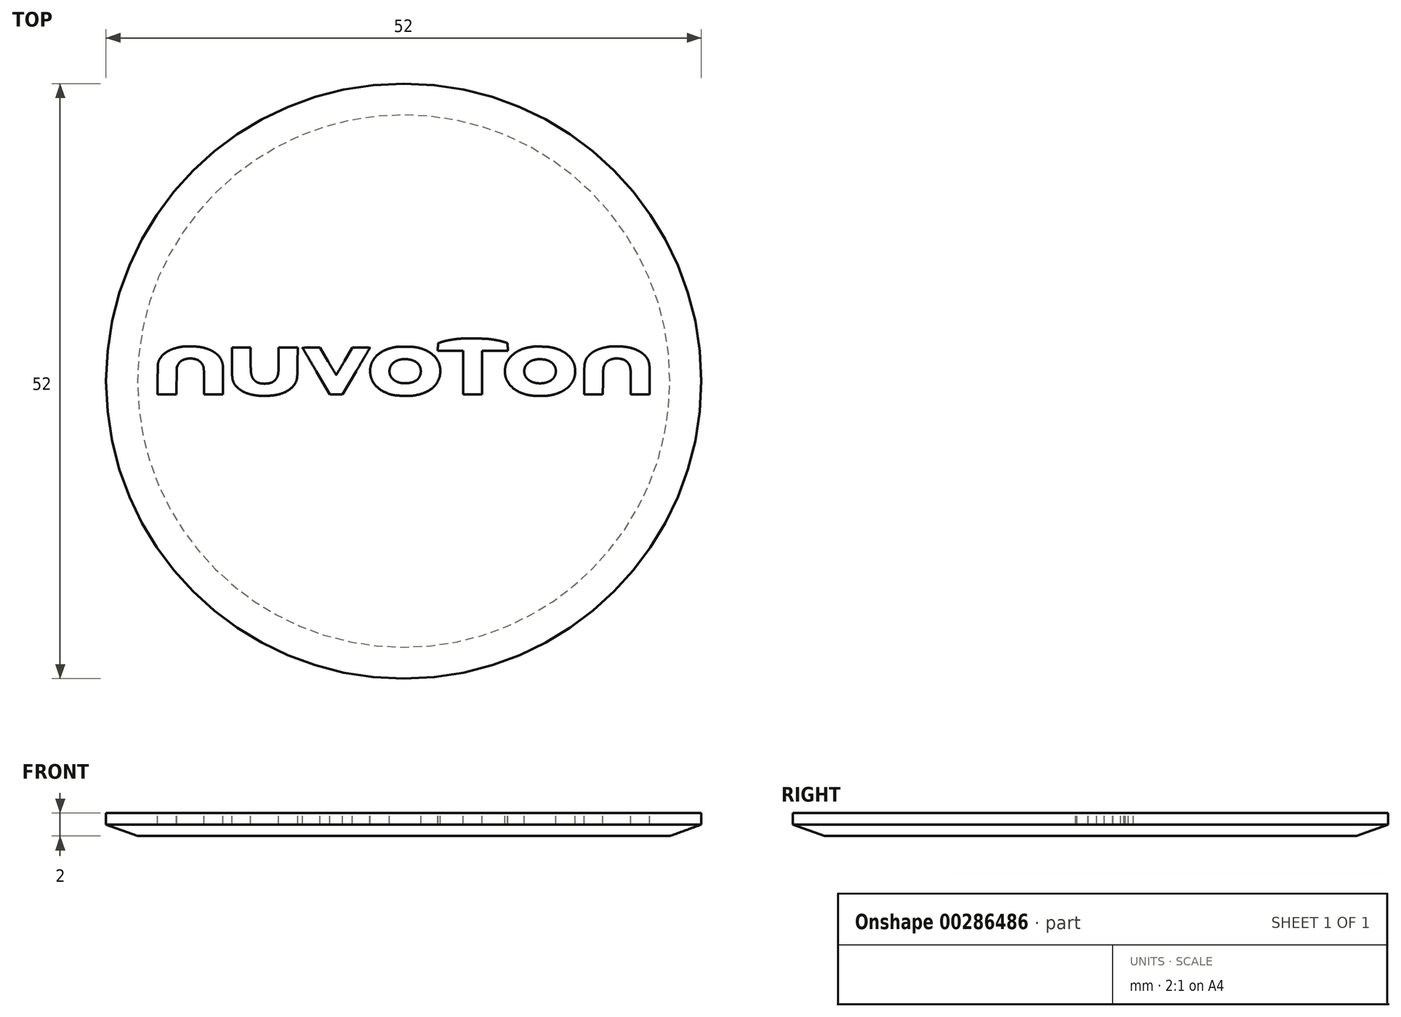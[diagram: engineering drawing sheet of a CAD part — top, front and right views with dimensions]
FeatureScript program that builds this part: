
annotation { "Feature Type Name" : "Feature", "Feature Type Description" : "" }
export const myFeature = defineFeature(function(context is Context, id is Id, definition is map)
    precondition{}
    {
        {
            var Q0;
            Q0=qCreatedBy(makeId("Top.planeOp"),FACE);
            var sketch = newSketch(context, id + "F0", { "sketchPlane" : qUnion([Q0])});
            skCircle(sketch, "E0", {"center": v(0, 0) * mm, "radius": 26 * mm});
            skSolve(sketch);
        }
        {
            var Q0;
            Q0 = qSketchRegion(id + "F0", true);
            extrude(context, id + "F1", {"entities" : qUnion([Q0]), "depth" : 2 * mm, "offsetDistance" : 25 * mm});
        }
        {
            var Q0;
            Q0=makeQuery(id+"F1.opExtrude","CAP_EDGE",EDGE,{"disambiguationData":[OSD([sQuery(id+"F0.wireOp",EDGE,"E0")])],"isStart":true});
            chamfer(context, id + "F2", {"entities" : qUnion([Q0]), "chamferType" : ChamferType.OFFSET_ANGLE, "width" : 1 * mm, "oppositeDirection" : false, "angle" : 70 * degree, "tangentPropagation" : true});
        }
        {
            var Q0;
            Q0=makeQuery(id+"F1.opExtrude","CAP_FACE",FACE,{"disambiguationData":[OSD([sQuery(id+"F0.wireOp",EDGE,"E0")])],"isStart":false});
            var sketch = newSketch(context, id + "F3", { "sketchPlane" : qUnion([Q0])});
            skArc(sketch, "E1", {"start": v(4.94, 3.7) * mm, "mid": v(4.7, 3.68) * mm, "end": v(4.45, 3.65) * mm});
            skArc(sketch, "E2", {"start": v(4.45, 3.65) * mm, "mid": v(4.22, 3.62) * mm, "end": v(4, 3.58) * mm});
            skArc(sketch, "E3", {"start": v(4, 3.58) * mm, "mid": v(3.78, 3.54) * mm, "end": v(3.58, 3.5) * mm});
            skArc(sketch, "E4", {"start": v(3.58, 3.5) * mm, "mid": v(3.4, 3.44) * mm, "end": v(3.22, 3.39) * mm});
            skLineSegment(sketch, "E5", {"start": v(3.22, 3.39) * mm, "end": v(3, 3.31) * mm});
            skLineSegment(sketch, "E6", {"start": v(3, 3.31) * mm, "end": v(3, 2.98) * mm});
            skLineSegment(sketch, "E7", {"start": v(3, 2.98) * mm, "end": v(2.99, 2.64) * mm});
            skLineSegment(sketch, "E8", {"start": v(2.99, 2.64) * mm, "end": v(4.1, 2.64) * mm});
            skLineSegment(sketch, "E9", {"start": v(4.1, 2.64) * mm, "end": v(5.2, 2.64) * mm});
            skLineSegment(sketch, "E10", {"start": v(5.2, 2.64) * mm, "end": v(5.2, 0.74) * mm});
            skLineSegment(sketch, "E11", {"start": v(5.2, 0.74) * mm, "end": v(5.2, -1.17) * mm});
            skLineSegment(sketch, "E12", {"start": v(5.2, -1.17) * mm, "end": v(6.04, -1.17) * mm});
            skLineSegment(sketch, "E13", {"start": v(6.04, -1.17) * mm, "end": v(6.87, -1.17) * mm});
            skLineSegment(sketch, "E14", {"start": v(6.87, -1.17) * mm, "end": v(6.87, 0.74) * mm});
            skLineSegment(sketch, "E15", {"start": v(6.87, 0.74) * mm, "end": v(6.87, 2.64) * mm});
            skLineSegment(sketch, "E16", {"start": v(6.87, 2.64) * mm, "end": v(7.98, 2.64) * mm});
            skLineSegment(sketch, "E17", {"start": v(7.98, 2.64) * mm, "end": v(9.09, 2.64) * mm});
            skLineSegment(sketch, "E18", {"start": v(9.09, 2.64) * mm, "end": v(9.08, 2.98) * mm});
            skLineSegment(sketch, "E19", {"start": v(9.08, 2.98) * mm, "end": v(9.07, 3.32) * mm});
            skLineSegment(sketch, "E20", {"start": v(9.07, 3.32) * mm, "end": v(8.82, 3.4) * mm});
            skArc(sketch, "E21", {"start": v(8.82, 3.4) * mm, "mid": v(8.7, 3.44) * mm, "end": v(8.56, 3.48) * mm});
            skArc(sketch, "E22", {"start": v(8.56, 3.48) * mm, "mid": v(8.41, 3.51) * mm, "end": v(8.26, 3.55) * mm});
            skArc(sketch, "E23", {"start": v(8.26, 3.55) * mm, "mid": v(8.09, 3.58) * mm, "end": v(7.92, 3.6) * mm});
            skArc(sketch, "E24", {"start": v(7.92, 3.6) * mm, "mid": v(7.74, 3.64) * mm, "end": v(7.55, 3.66) * mm});
            skArc(sketch, "E25", {"start": v(7.55, 3.66) * mm, "mid": v(7.32, 3.69) * mm, "end": v(7.09, 3.7) * mm});
            skArc(sketch, "E26", {"start": v(7.09, 3.7) * mm, "mid": v(6.68, 3.71) * mm, "end": v(6.26, 3.72) * mm});
            skArc(sketch, "E27", {"start": v(6.26, 3.72) * mm, "mid": v(5.85, 3.73) * mm, "end": v(5.44, 3.73) * mm});
            skArc(sketch, "E28", {"start": v(5.44, 3.73) * mm, "mid": v(5.19, 3.72) * mm, "end": v(4.94, 3.7) * mm});
            skArc(sketch, "E29", {"start": v(-19.23, 3.02) * mm, "mid": v(-19.63, 2.95) * mm, "end": v(-20.03, 2.85) * mm});
            skArc(sketch, "E30", {"start": v(-20.03, 2.85) * mm, "mid": v(-20.35, 2.74) * mm, "end": v(-20.66, 2.58) * mm});
            skArc(sketch, "E31", {"start": v(-20.66, 2.58) * mm, "mid": v(-20.9, 2.4) * mm, "end": v(-21.12, 2.2) * mm});
            skArc(sketch, "E32", {"start": v(-21.12, 2.2) * mm, "mid": v(-21.3, 1.97) * mm, "end": v(-21.41, 1.71) * mm});
            skArc(sketch, "E33", {"start": v(-21.41, 1.71) * mm, "mid": v(-21.44, 1.64) * mm, "end": v(-21.45, 1.56) * mm});
            skArc(sketch, "E34", {"start": v(-21.45, 1.56) * mm, "mid": v(-21.47, 1.47) * mm, "end": v(-21.47, 1.37) * mm});
            skArc(sketch, "E35", {"start": v(-21.47, 1.37) * mm, "mid": v(-21.48, 1.2) * mm, "end": v(-21.48, 1.03) * mm});
            skArc(sketch, "E36", {"start": v(-21.48, 1.03) * mm, "mid": v(-21.49, 0.6) * mm, "end": v(-21.5, 0.18) * mm});
            skLineSegment(sketch, "E37", {"start": v(-21.5, 0.18) * mm, "end": v(-21.5, -1.17) * mm});
            skLineSegment(sketch, "E38", {"start": v(-21.5, -1.17) * mm, "end": v(-20.67, -1.17) * mm});
            skLineSegment(sketch, "E39", {"start": v(-20.67, -1.17) * mm, "end": v(-19.84, -1.17) * mm});
            skLineSegment(sketch, "E40", {"start": v(-19.84, -1.17) * mm, "end": v(-19.83, 0.01) * mm});
            skLineSegment(sketch, "E41", {"start": v(-19.83, 0.01) * mm, "end": v(-19.82, 1.2) * mm});
            skLineSegment(sketch, "E42", {"start": v(-19.82, 1.2) * mm, "end": v(-19.72, 1.4) * mm});
            skArc(sketch, "E43", {"start": v(-19.72, 1.4) * mm, "mid": v(-19.7, 1.44) * mm, "end": v(-19.67, 1.49) * mm});
            skArc(sketch, "E44", {"start": v(-19.67, 1.49) * mm, "mid": v(-19.65, 1.53) * mm, "end": v(-19.62, 1.57) * mm});
            skArc(sketch, "E45", {"start": v(-19.62, 1.57) * mm, "mid": v(-19.6, 1.61) * mm, "end": v(-19.56, 1.65) * mm});
            skArc(sketch, "E46", {"start": v(-19.56, 1.65) * mm, "mid": v(-19.54, 1.67) * mm, "end": v(-19.52, 1.7) * mm});
            skArc(sketch, "E47", {"start": v(-19.52, 1.7) * mm, "mid": v(-19.41, 1.77) * mm, "end": v(-19.3, 1.84) * mm});
            skArc(sketch, "E48", {"start": v(-19.3, 1.84) * mm, "mid": v(-19.16, 1.9) * mm, "end": v(-19.02, 1.93) * mm});
            skArc(sketch, "E49", {"start": v(-19.02, 1.93) * mm, "mid": v(-18.87, 1.96) * mm, "end": v(-18.72, 1.98) * mm});
            skArc(sketch, "E50", {"start": v(-18.72, 1.98) * mm, "mid": v(-18.57, 1.98) * mm, "end": v(-18.42, 1.96) * mm});
            skArc(sketch, "E51", {"start": v(-18.42, 1.96) * mm, "mid": v(-18.3, 1.94) * mm, "end": v(-18.19, 1.91) * mm});
            skArc(sketch, "E52", {"start": v(-18.19, 1.91) * mm, "mid": v(-18.1, 1.89) * mm, "end": v(-18, 1.85) * mm});
            skArc(sketch, "E53", {"start": v(-18, 1.85) * mm, "mid": v(-17.93, 1.8) * mm, "end": v(-17.86, 1.76) * mm});
            skArc(sketch, "E54", {"start": v(-17.86, 1.76) * mm, "mid": v(-17.78, 1.7) * mm, "end": v(-17.72, 1.63) * mm});
            skArc(sketch, "E55", {"start": v(-17.72, 1.63) * mm, "mid": v(-17.63, 1.52) * mm, "end": v(-17.56, 1.41) * mm});
            skArc(sketch, "E56", {"start": v(-17.56, 1.41) * mm, "mid": v(-17.51, 1.31) * mm, "end": v(-17.48, 1.2) * mm});
            skArc(sketch, "E57", {"start": v(-17.48, 1.2) * mm, "mid": v(-17.46, 1.04) * mm, "end": v(-17.45, 0.87) * mm});
            skArc(sketch, "E58", {"start": v(-17.45, 0.87) * mm, "mid": v(-17.44, 0.43) * mm, "end": v(-17.44, 0) * mm});
            skLineSegment(sketch, "E59", {"start": v(-17.44, 0) * mm, "end": v(-17.43, -1.17) * mm});
            skLineSegment(sketch, "E60", {"start": v(-17.43, -1.17) * mm, "end": v(-16.6, -1.17) * mm});
            skLineSegment(sketch, "E61", {"start": v(-16.6, -1.17) * mm, "end": v(-15.77, -1.17) * mm});
            skLineSegment(sketch, "E62", {"start": v(-15.77, -1.17) * mm, "end": v(-15.78, 0.03) * mm});
            skArc(sketch, "E63", {"start": v(-15.78, 0.03) * mm, "mid": v(-15.78, 0.26) * mm, "end": v(-15.78, 0.5) * mm});
            skArc(sketch, "E64", {"start": v(-15.78, 0.5) * mm, "mid": v(-15.78, 0.72) * mm, "end": v(-15.78, 0.93) * mm});
            skArc(sketch, "E65", {"start": v(-15.78, 0.93) * mm, "mid": v(-15.79, 1.11) * mm, "end": v(-15.8, 1.3) * mm});
            skArc(sketch, "E66", {"start": v(-15.8, 1.3) * mm, "mid": v(-15.8, 1.37) * mm, "end": v(-15.8, 1.43) * mm});
            skArc(sketch, "E67", {"start": v(-15.8, 1.43) * mm, "mid": v(-15.85, 1.63) * mm, "end": v(-15.91, 1.81) * mm});
            skArc(sketch, "E68", {"start": v(-15.91, 1.81) * mm, "mid": v(-16, 1.99) * mm, "end": v(-16.12, 2.15) * mm});
            skArc(sketch, "E69", {"start": v(-16.12, 2.15) * mm, "mid": v(-16.26, 2.3) * mm, "end": v(-16.42, 2.44) * mm});
            skArc(sketch, "E70", {"start": v(-16.42, 2.44) * mm, "mid": v(-16.61, 2.56) * mm, "end": v(-16.81, 2.67) * mm});
            skArc(sketch, "E71", {"start": v(-16.81, 2.67) * mm, "mid": v(-17, 2.76) * mm, "end": v(-17.2, 2.83) * mm});
            skArc(sketch, "E72", {"start": v(-17.2, 2.83) * mm, "mid": v(-17.39, 2.9) * mm, "end": v(-17.58, 2.94) * mm});
            skArc(sketch, "E73", {"start": v(-17.58, 2.94) * mm, "mid": v(-17.8, 2.98) * mm, "end": v(-18.01, 3) * mm});
            skArc(sketch, "E74", {"start": v(-18.01, 3) * mm, "mid": v(-18.27, 3.02) * mm, "end": v(-18.53, 3.04) * mm});
            skArc(sketch, "E75", {"start": v(-18.53, 3.04) * mm, "mid": v(-18.63, 3.04) * mm, "end": v(-18.73, 3.04) * mm});
            skArc(sketch, "E76", {"start": v(-18.73, 3.04) * mm, "mid": v(-18.83, 3.04) * mm, "end": v(-18.93, 3.04) * mm});
            skArc(sketch, "E77", {"start": v(-18.93, 3.04) * mm, "mid": v(-19.02, 3.03) * mm, "end": v(-19.12, 3.03) * mm});
            skArc(sketch, "E78", {"start": v(-19.12, 3.03) * mm, "mid": v(-19.17, 3.03) * mm, "end": v(-19.23, 3.02) * mm});
            skArc(sketch, "E79", {"start": v(18.05, 3.02) * mm, "mid": v(17.84, 3) * mm, "end": v(17.63, 2.95) * mm});
            skArc(sketch, "E80", {"start": v(17.63, 2.95) * mm, "mid": v(17.44, 2.9) * mm, "end": v(17.24, 2.85) * mm});
            skArc(sketch, "E81", {"start": v(17.24, 2.85) * mm, "mid": v(17.07, 2.8) * mm, "end": v(16.9, 2.73) * mm});
            skArc(sketch, "E82", {"start": v(16.9, 2.73) * mm, "mid": v(16.75, 2.66) * mm, "end": v(16.6, 2.58) * mm});
            skArc(sketch, "E83", {"start": v(16.6, 2.58) * mm, "mid": v(16.51, 2.52) * mm, "end": v(16.42, 2.45) * mm});
            skArc(sketch, "E84", {"start": v(16.42, 2.45) * mm, "mid": v(16.33, 2.37) * mm, "end": v(16.23, 2.28) * mm});
            skArc(sketch, "E85", {"start": v(16.23, 2.28) * mm, "mid": v(16.15, 2.2) * mm, "end": v(16.07, 2.1) * mm});
            skArc(sketch, "E86", {"start": v(16.07, 2.1) * mm, "mid": v(16, 2.02) * mm, "end": v(15.96, 1.94) * mm});
            skArc(sketch, "E87", {"start": v(15.96, 1.94) * mm, "mid": v(15.9, 1.82) * mm, "end": v(15.86, 1.7) * mm});
            skArc(sketch, "E88", {"start": v(15.86, 1.7) * mm, "mid": v(15.82, 1.57) * mm, "end": v(15.8, 1.44) * mm});
            skArc(sketch, "E89", {"start": v(15.8, 1.44) * mm, "mid": v(15.79, 1.24) * mm, "end": v(15.78, 1.04) * mm});
            skArc(sketch, "E90", {"start": v(15.78, 1.04) * mm, "mid": v(15.78, 0.58) * mm, "end": v(15.78, 0.12) * mm});
            skLineSegment(sketch, "E91", {"start": v(15.78, 0.12) * mm, "end": v(15.78, -1.17) * mm});
            skLineSegment(sketch, "E92", {"start": v(15.78, -1.17) * mm, "end": v(16.59, -1.17) * mm});
            skLineSegment(sketch, "E93", {"start": v(16.59, -1.17) * mm, "end": v(17.4, -1.17) * mm});
            skLineSegment(sketch, "E94", {"start": v(17.4, -1.17) * mm, "end": v(17.41, -0.04) * mm});
            skArc(sketch, "E95", {"start": v(17.41, -0.04) * mm, "mid": v(17.42, 0.37) * mm, "end": v(17.43, 0.78) * mm});
            skArc(sketch, "E96", {"start": v(17.43, 0.78) * mm, "mid": v(17.44, 0.96) * mm, "end": v(17.45, 1.14) * mm});
            skArc(sketch, "E97", {"start": v(17.45, 1.14) * mm, "mid": v(17.48, 1.25) * mm, "end": v(17.52, 1.36) * mm});
            skArc(sketch, "E98", {"start": v(17.52, 1.36) * mm, "mid": v(17.57, 1.46) * mm, "end": v(17.63, 1.56) * mm});
            skArc(sketch, "E99", {"start": v(17.63, 1.56) * mm, "mid": v(17.7, 1.64) * mm, "end": v(17.79, 1.72) * mm});
            skArc(sketch, "E100", {"start": v(17.79, 1.72) * mm, "mid": v(17.88, 1.78) * mm, "end": v(17.97, 1.84) * mm});
            skArc(sketch, "E101", {"start": v(17.97, 1.84) * mm, "mid": v(18.08, 1.89) * mm, "end": v(18.2, 1.92) * mm});
            skArc(sketch, "E102", {"start": v(18.2, 1.92) * mm, "mid": v(18.33, 1.95) * mm, "end": v(18.47, 1.97) * mm});
            skArc(sketch, "E103", {"start": v(18.47, 1.97) * mm, "mid": v(18.56, 1.98) * mm, "end": v(18.65, 1.98) * mm});
            skArc(sketch, "E104", {"start": v(18.65, 1.98) * mm, "mid": v(18.76, 1.97) * mm, "end": v(18.86, 1.96) * mm});
            skArc(sketch, "E105", {"start": v(18.86, 1.96) * mm, "mid": v(18.97, 1.94) * mm, "end": v(19.08, 1.92) * mm});
            skArc(sketch, "E106", {"start": v(19.08, 1.92) * mm, "mid": v(19.16, 1.9) * mm, "end": v(19.23, 1.87) * mm});
            skArc(sketch, "E107", {"start": v(19.23, 1.87) * mm, "mid": v(19.3, 1.83) * mm, "end": v(19.37, 1.79) * mm});
            skArc(sketch, "E108", {"start": v(19.37, 1.79) * mm, "mid": v(19.44, 1.74) * mm, "end": v(19.5, 1.68) * mm});
            skArc(sketch, "E109", {"start": v(19.5, 1.68) * mm, "mid": v(19.56, 1.62) * mm, "end": v(19.62, 1.55) * mm});
            skArc(sketch, "E110", {"start": v(19.62, 1.55) * mm, "mid": v(19.66, 1.5) * mm, "end": v(19.7, 1.43) * mm});
            skArc(sketch, "E111", {"start": v(19.7, 1.43) * mm, "mid": v(19.74, 1.33) * mm, "end": v(19.78, 1.22) * mm});
            skArc(sketch, "E112", {"start": v(19.78, 1.22) * mm, "mid": v(19.8, 1.1) * mm, "end": v(19.82, 0.97) * mm});
            skArc(sketch, "E113", {"start": v(19.82, 0.97) * mm, "mid": v(19.83, 0.78) * mm, "end": v(19.84, 0.6) * mm});
            skArc(sketch, "E114", {"start": v(19.84, 0.6) * mm, "mid": v(19.84, 0.23) * mm, "end": v(19.84, -0.13) * mm});
            skLineSegment(sketch, "E115", {"start": v(19.84, -0.13) * mm, "end": v(19.84, -1.17) * mm});
            skLineSegment(sketch, "E116", {"start": v(19.84, -1.17) * mm, "end": v(20.67, -1.17) * mm});
            skLineSegment(sketch, "E117", {"start": v(20.67, -1.17) * mm, "end": v(21.5, -1.17) * mm});
            skLineSegment(sketch, "E118", {"start": v(21.5, -1.17) * mm, "end": v(21.5, 0.01) * mm});
            skArc(sketch, "E119", {"start": v(21.5, 0.01) * mm, "mid": v(21.5, 0.41) * mm, "end": v(21.5, 0.81) * mm});
            skArc(sketch, "E120", {"start": v(21.5, 0.81) * mm, "mid": v(21.49, 1.03) * mm, "end": v(21.48, 1.25) * mm});
            skArc(sketch, "E121", {"start": v(21.48, 1.25) * mm, "mid": v(21.46, 1.4) * mm, "end": v(21.44, 1.54) * mm});
            skArc(sketch, "E122", {"start": v(21.44, 1.54) * mm, "mid": v(21.41, 1.66) * mm, "end": v(21.38, 1.77) * mm});
            skArc(sketch, "E123", {"start": v(21.38, 1.77) * mm, "mid": v(21.31, 1.9) * mm, "end": v(21.24, 2.04) * mm});
            skArc(sketch, "E124", {"start": v(21.24, 2.04) * mm, "mid": v(21.14, 2.16) * mm, "end": v(21.03, 2.28) * mm});
            skArc(sketch, "E125", {"start": v(21.03, 2.28) * mm, "mid": v(20.9, 2.4) * mm, "end": v(20.75, 2.5) * mm});
            skArc(sketch, "E126", {"start": v(20.75, 2.5) * mm, "mid": v(20.59, 2.6) * mm, "end": v(20.42, 2.7) * mm});
            skArc(sketch, "E127", {"start": v(20.42, 2.7) * mm, "mid": v(20.24, 2.77) * mm, "end": v(20.05, 2.84) * mm});
            skArc(sketch, "E128", {"start": v(20.05, 2.84) * mm, "mid": v(19.87, 2.9) * mm, "end": v(19.68, 2.94) * mm});
            skArc(sketch, "E129", {"start": v(19.68, 2.94) * mm, "mid": v(19.46, 2.98) * mm, "end": v(19.25, 3) * mm});
            skArc(sketch, "E130", {"start": v(19.25, 3) * mm, "mid": v(19, 3.02) * mm, "end": v(18.75, 3.04) * mm});
            skArc(sketch, "E131", {"start": v(18.75, 3.04) * mm, "mid": v(18.65, 3.04) * mm, "end": v(18.55, 3.04) * mm});
            skArc(sketch, "E132", {"start": v(18.55, 3.04) * mm, "mid": v(18.45, 3.04) * mm, "end": v(18.34, 3.04) * mm});
            skArc(sketch, "E133", {"start": v(18.34, 3.04) * mm, "mid": v(18.25, 3.03) * mm, "end": v(18.16, 3.03) * mm});
            skArc(sketch, "E134", {"start": v(18.16, 3.03) * mm, "mid": v(18.1, 3.03) * mm, "end": v(18.05, 3.02) * mm});
            skArc(sketch, "E135", {"start": v(-0.66, 2.99) * mm, "mid": v(-1.13, 2.88) * mm, "end": v(-1.6, 2.72) * mm});
            skArc(sketch, "E136", {"start": v(-1.6, 2.72) * mm, "mid": v(-1.97, 2.52) * mm, "end": v(-2.32, 2.26) * mm});
            skArc(sketch, "E137", {"start": v(-2.32, 2.26) * mm, "mid": v(-2.57, 1.96) * mm, "end": v(-2.77, 1.63) * mm});
            skArc(sketch, "E138", {"start": v(-2.77, 1.63) * mm, "mid": v(-2.9, 1.26) * mm, "end": v(-2.93, 0.88) * mm});
            skArc(sketch, "E139", {"start": v(-2.93, 0.88) * mm, "mid": v(-2.9, 0.52) * mm, "end": v(-2.8, 0.17) * mm});
            skArc(sketch, "E140", {"start": v(-2.8, 0.17) * mm, "mid": v(-2.63, -0.15) * mm, "end": v(-2.4, -0.44) * mm});
            skArc(sketch, "E141", {"start": v(-2.4, -0.44) * mm, "mid": v(-2.12, -0.7) * mm, "end": v(-1.78, -0.9) * mm});
            skArc(sketch, "E142", {"start": v(-1.78, -0.9) * mm, "mid": v(-1.38, -1.08) * mm, "end": v(-0.96, -1.2) * mm});
            skArc(sketch, "E143", {"start": v(-0.96, -1.2) * mm, "mid": v(-0.79, -1.24) * mm, "end": v(-0.62, -1.26) * mm});
            skArc(sketch, "E144", {"start": v(-0.62, -1.26) * mm, "mid": v(-0.34, -1.28) * mm, "end": v(-0.06, -1.29) * mm});
            skArc(sketch, "E145", {"start": v(-0.06, -1.29) * mm, "mid": v(0.22, -1.3) * mm, "end": v(0.5, -1.3) * mm});
            skArc(sketch, "E146", {"start": v(0.5, -1.3) * mm, "mid": v(0.68, -1.29) * mm, "end": v(0.87, -1.27) * mm});
            skArc(sketch, "E147", {"start": v(0.87, -1.27) * mm, "mid": v(1.36, -1.16) * mm, "end": v(1.84, -1) * mm});
            skArc(sketch, "E148", {"start": v(1.84, -1) * mm, "mid": v(2.23, -0.8) * mm, "end": v(2.58, -0.54) * mm});
            skArc(sketch, "E149", {"start": v(2.58, -0.54) * mm, "mid": v(2.84, -0.24) * mm, "end": v(3.04, 0.1) * mm});
            skArc(sketch, "E150", {"start": v(3.04, 0.1) * mm, "mid": v(3.16, 0.47) * mm, "end": v(3.2, 0.86) * mm});
            skArc(sketch, "E151", {"start": v(3.2, 0.86) * mm, "mid": v(3.18, 1.18) * mm, "end": v(3.1, 1.48) * mm});
            skArc(sketch, "E152", {"start": v(3.1, 1.48) * mm, "mid": v(2.97, 1.77) * mm, "end": v(2.8, 2.03) * mm});
            skArc(sketch, "E153", {"start": v(2.8, 2.03) * mm, "mid": v(2.57, 2.28) * mm, "end": v(2.3, 2.48) * mm});
            skArc(sketch, "E154", {"start": v(2.3, 2.48) * mm, "mid": v(2, 2.66) * mm, "end": v(1.66, 2.8) * mm});
            skArc(sketch, "E155", {"start": v(1.66, 2.8) * mm, "mid": v(1.5, 2.86) * mm, "end": v(1.34, 2.9) * mm});
            skArc(sketch, "E156", {"start": v(1.34, 2.9) * mm, "mid": v(1.2, 2.93) * mm, "end": v(1.05, 2.96) * mm});
            skArc(sketch, "E157", {"start": v(1.05, 2.96) * mm, "mid": v(0.89, 2.98) * mm, "end": v(0.72, 3) * mm});
            skArc(sketch, "E158", {"start": v(0.72, 3) * mm, "mid": v(0.48, 3) * mm, "end": v(0.24, 3) * mm});
            skArc(sketch, "E159", {"start": v(0.24, 3) * mm, "mid": v(0.1, 3) * mm, "end": v(-0.05, 3) * mm});
            skArc(sketch, "E160", {"start": v(-0.05, 3) * mm, "mid": v(-0.18, 3) * mm, "end": v(-0.32, 3) * mm});
            skArc(sketch, "E161", {"start": v(-0.32, 3) * mm, "mid": v(-0.43, 3) * mm, "end": v(-0.54, 3) * mm});
            skArc(sketch, "E162", {"start": v(-0.54, 3) * mm, "mid": v(-0.6, 3) * mm, "end": v(-0.66, 2.99) * mm});
            skArc(sketch, "E163", {"start": v(0.52, 1.88) * mm, "mid": v(0.73, 1.83) * mm, "end": v(0.93, 1.75) * mm});
            skArc(sketch, "E164", {"start": v(0.93, 1.75) * mm, "mid": v(1.1, 1.66) * mm, "end": v(1.24, 1.53) * mm});
            skArc(sketch, "E165", {"start": v(1.24, 1.53) * mm, "mid": v(1.35, 1.39) * mm, "end": v(1.43, 1.23) * mm});
            skArc(sketch, "E166", {"start": v(1.43, 1.23) * mm, "mid": v(1.48, 1.05) * mm, "end": v(1.5, 0.86) * mm});
            skArc(sketch, "E167", {"start": v(1.5, 0.86) * mm, "mid": v(1.48, 0.65) * mm, "end": v(1.42, 0.45) * mm});
            skArc(sketch, "E168", {"start": v(1.42, 0.45) * mm, "mid": v(1.31, 0.27) * mm, "end": v(1.17, 0.13) * mm});
            skArc(sketch, "E169", {"start": v(1.17, 0.13) * mm, "mid": v(0.99, 0) * mm, "end": v(0.78, -0.1) * mm});
            skArc(sketch, "E170", {"start": v(0.78, -0.1) * mm, "mid": v(0.52, -0.16) * mm, "end": v(0.26, -0.19) * mm});
            skArc(sketch, "E171", {"start": v(0.26, -0.19) * mm, "mid": v(0.02, -0.2) * mm, "end": v(-0.21, -0.17) * mm});
            skArc(sketch, "E172", {"start": v(-0.21, -0.17) * mm, "mid": v(-0.42, -0.12) * mm, "end": v(-0.62, -0.04) * mm});
            skArc(sketch, "E173", {"start": v(-0.62, -0.04) * mm, "mid": v(-0.8, 0.05) * mm, "end": v(-0.94, 0.17) * mm});
            skArc(sketch, "E174", {"start": v(-0.94, 0.17) * mm, "mid": v(-1.07, 0.3) * mm, "end": v(-1.16, 0.47) * mm});
            skArc(sketch, "E175", {"start": v(-1.16, 0.47) * mm, "mid": v(-1.2, 0.56) * mm, "end": v(-1.22, 0.66) * mm});
            skArc(sketch, "E176", {"start": v(-1.22, 0.66) * mm, "mid": v(-1.24, 0.77) * mm, "end": v(-1.24, 0.88) * mm});
            skArc(sketch, "E177", {"start": v(-1.24, 0.88) * mm, "mid": v(-1.23, 0.99) * mm, "end": v(-1.21, 1.1) * mm});
            skArc(sketch, "E178", {"start": v(-1.21, 1.1) * mm, "mid": v(-1.18, 1.2) * mm, "end": v(-1.14, 1.3) * mm});
            skArc(sketch, "E179", {"start": v(-1.14, 1.3) * mm, "mid": v(-1.03, 1.47) * mm, "end": v(-0.88, 1.6) * mm});
            skArc(sketch, "E180", {"start": v(-0.88, 1.6) * mm, "mid": v(-0.7, 1.73) * mm, "end": v(-0.5, 1.82) * mm});
            skArc(sketch, "E181", {"start": v(-0.5, 1.82) * mm, "mid": v(-0.26, 1.89) * mm, "end": v(-0.02, 1.92) * mm});
            skArc(sketch, "E182", {"start": v(-0.02, 1.92) * mm, "mid": v(0.25, 1.91) * mm, "end": v(0.52, 1.88) * mm});
            skArc(sketch, "E183", {"start": v(11.27, 3) * mm, "mid": v(11.26, 3) * mm, "end": v(11.24, 3) * mm});
            skArc(sketch, "E184", {"start": v(11.24, 3) * mm, "mid": v(11.2, 3) * mm, "end": v(11.17, 2.99) * mm});
            skArc(sketch, "E185", {"start": v(11.17, 2.99) * mm, "mid": v(11.13, 2.98) * mm, "end": v(11.09, 2.97) * mm});
            skArc(sketch, "E186", {"start": v(11.09, 2.97) * mm, "mid": v(11.04, 2.96) * mm, "end": v(11, 2.96) * mm});
            skArc(sketch, "E187", {"start": v(11, 2.96) * mm, "mid": v(10.63, 2.88) * mm, "end": v(10.28, 2.76) * mm});
            skArc(sketch, "E188", {"start": v(10.28, 2.76) * mm, "mid": v(9.96, 2.6) * mm, "end": v(9.66, 2.42) * mm});
            skArc(sketch, "E189", {"start": v(9.66, 2.42) * mm, "mid": v(9.42, 2.2) * mm, "end": v(9.2, 1.96) * mm});
            skArc(sketch, "E190", {"start": v(9.2, 1.96) * mm, "mid": v(9.04, 1.7) * mm, "end": v(8.92, 1.4) * mm});
            skArc(sketch, "E191", {"start": v(8.92, 1.4) * mm, "mid": v(8.89, 1.28) * mm, "end": v(8.87, 1.15) * mm});
            skArc(sketch, "E192", {"start": v(8.87, 1.15) * mm, "mid": v(8.85, 1) * mm, "end": v(8.85, 0.85) * mm});
            skArc(sketch, "E193", {"start": v(8.85, 0.85) * mm, "mid": v(8.86, 0.7) * mm, "end": v(8.87, 0.54) * mm});
            skArc(sketch, "E194", {"start": v(8.87, 0.54) * mm, "mid": v(8.9, 0.42) * mm, "end": v(8.93, 0.3) * mm});
            skArc(sketch, "E195", {"start": v(8.93, 0.3) * mm, "mid": v(9.05, 0) * mm, "end": v(9.23, -0.26) * mm});
            skArc(sketch, "E196", {"start": v(9.23, -0.26) * mm, "mid": v(9.44, -0.5) * mm, "end": v(9.7, -0.72) * mm});
            skArc(sketch, "E197", {"start": v(9.7, -0.72) * mm, "mid": v(10, -0.9) * mm, "end": v(10.31, -1.05) * mm});
            skArc(sketch, "E198", {"start": v(10.31, -1.05) * mm, "mid": v(10.68, -1.17) * mm, "end": v(11.07, -1.25) * mm});
            skArc(sketch, "E199", {"start": v(11.07, -1.25) * mm, "mid": v(11.23, -1.27) * mm, "end": v(11.39, -1.28) * mm});
            skArc(sketch, "E200", {"start": v(11.39, -1.28) * mm, "mid": v(11.63, -1.29) * mm, "end": v(11.88, -1.3) * mm});
            skArc(sketch, "E201", {"start": v(11.88, -1.3) * mm, "mid": v(12.13, -1.3) * mm, "end": v(12.37, -1.29) * mm});
            skArc(sketch, "E202", {"start": v(12.37, -1.29) * mm, "mid": v(12.53, -1.28) * mm, "end": v(12.7, -1.26) * mm});
            skArc(sketch, "E203", {"start": v(12.7, -1.26) * mm, "mid": v(12.84, -1.24) * mm, "end": v(12.98, -1.2) * mm});
            skArc(sketch, "E204", {"start": v(12.98, -1.2) * mm, "mid": v(13.11, -1.18) * mm, "end": v(13.24, -1.14) * mm});
            skArc(sketch, "E205", {"start": v(13.24, -1.14) * mm, "mid": v(13.37, -1.1) * mm, "end": v(13.5, -1.05) * mm});
            skArc(sketch, "E206", {"start": v(13.5, -1.05) * mm, "mid": v(13.63, -1) * mm, "end": v(13.76, -0.93) * mm});
            skArc(sketch, "E207", {"start": v(13.76, -0.93) * mm, "mid": v(13.97, -0.82) * mm, "end": v(14.16, -0.7) * mm});
            skArc(sketch, "E208", {"start": v(14.16, -0.7) * mm, "mid": v(14.34, -0.56) * mm, "end": v(14.5, -0.4) * mm});
            skArc(sketch, "E209", {"start": v(14.5, -0.4) * mm, "mid": v(14.63, -0.24) * mm, "end": v(14.74, -0.07) * mm});
            skArc(sketch, "E210", {"start": v(14.74, -0.07) * mm, "mid": v(14.84, 0.12) * mm, "end": v(14.9, 0.32) * mm});
            skArc(sketch, "E211", {"start": v(14.9, 0.32) * mm, "mid": v(14.94, 0.44) * mm, "end": v(14.96, 0.57) * mm});
            skArc(sketch, "E212", {"start": v(14.96, 0.57) * mm, "mid": v(14.98, 0.71) * mm, "end": v(14.98, 0.86) * mm});
            skArc(sketch, "E213", {"start": v(14.98, 0.86) * mm, "mid": v(14.98, 1.01) * mm, "end": v(14.96, 1.16) * mm});
            skArc(sketch, "E214", {"start": v(14.96, 1.16) * mm, "mid": v(14.94, 1.29) * mm, "end": v(14.9, 1.4) * mm});
            skArc(sketch, "E215", {"start": v(14.9, 1.4) * mm, "mid": v(14.8, 1.7) * mm, "end": v(14.62, 1.97) * mm});
            skArc(sketch, "E216", {"start": v(14.62, 1.97) * mm, "mid": v(14.4, 2.22) * mm, "end": v(14.15, 2.43) * mm});
            skArc(sketch, "E217", {"start": v(14.15, 2.43) * mm, "mid": v(13.85, 2.62) * mm, "end": v(13.52, 2.77) * mm});
            skArc(sketch, "E218", {"start": v(13.52, 2.77) * mm, "mid": v(13.14, 2.89) * mm, "end": v(12.74, 2.97) * mm});
            skArc(sketch, "E219", {"start": v(12.74, 2.97) * mm, "mid": v(12.6, 2.99) * mm, "end": v(12.47, 3) * mm});
            skArc(sketch, "E220", {"start": v(12.47, 3) * mm, "mid": v(12.22, 3) * mm, "end": v(11.97, 3.02) * mm});
            skArc(sketch, "E221", {"start": v(11.97, 3.02) * mm, "mid": v(11.72, 3.02) * mm, "end": v(11.47, 3.02) * mm});
            skArc(sketch, "E222", {"start": v(11.47, 3.02) * mm, "mid": v(11.37, 3.02) * mm, "end": v(11.27, 3) * mm});
            skArc(sketch, "E223", {"start": v(12.46, 1.85) * mm, "mid": v(12.62, 1.79) * mm, "end": v(12.78, 1.72) * mm});
            skArc(sketch, "E224", {"start": v(12.78, 1.72) * mm, "mid": v(12.9, 1.64) * mm, "end": v(13.02, 1.54) * mm});
            skArc(sketch, "E225", {"start": v(13.02, 1.54) * mm, "mid": v(13.11, 1.43) * mm, "end": v(13.18, 1.31) * mm});
            skArc(sketch, "E226", {"start": v(13.18, 1.31) * mm, "mid": v(13.24, 1.18) * mm, "end": v(13.28, 1.04) * mm});
            skArc(sketch, "E227", {"start": v(13.28, 1.04) * mm, "mid": v(13.3, 0.82) * mm, "end": v(13.26, 0.6) * mm});
            skArc(sketch, "E228", {"start": v(13.26, 0.6) * mm, "mid": v(13.18, 0.41) * mm, "end": v(13.06, 0.24) * mm});
            skArc(sketch, "E229", {"start": v(13.06, 0.24) * mm, "mid": v(12.9, 0.08) * mm, "end": v(12.7, -0.03) * mm});
            skArc(sketch, "E230", {"start": v(12.7, -0.03) * mm, "mid": v(12.45, -0.12) * mm, "end": v(12.2, -0.18) * mm});
            skArc(sketch, "E231", {"start": v(12.2, -0.18) * mm, "mid": v(11.95, -0.2) * mm, "end": v(11.7, -0.19) * mm});
            skArc(sketch, "E232", {"start": v(11.7, -0.19) * mm, "mid": v(11.47, -0.15) * mm, "end": v(11.25, -0.08) * mm});
            skArc(sketch, "E233", {"start": v(11.25, -0.08) * mm, "mid": v(11.06, 0) * mm, "end": v(10.88, 0.13) * mm});
            skArc(sketch, "E234", {"start": v(10.88, 0.13) * mm, "mid": v(10.74, 0.27) * mm, "end": v(10.63, 0.43) * mm});
            skArc(sketch, "E235", {"start": v(10.63, 0.43) * mm, "mid": v(10.6, 0.48) * mm, "end": v(10.59, 0.53) * mm});
            skArc(sketch, "E236", {"start": v(10.59, 0.53) * mm, "mid": v(10.57, 0.57) * mm, "end": v(10.56, 0.6) * mm});
            skArc(sketch, "E237", {"start": v(10.56, 0.6) * mm, "mid": v(10.55, 0.65) * mm, "end": v(10.55, 0.7) * mm});
            skArc(sketch, "E238", {"start": v(10.55, 0.7) * mm, "mid": v(10.55, 0.77) * mm, "end": v(10.54, 0.85) * mm});
            skArc(sketch, "E239", {"start": v(10.54, 0.85) * mm, "mid": v(10.54, 0.92) * mm, "end": v(10.55, 1) * mm});
            skArc(sketch, "E240", {"start": v(10.55, 1) * mm, "mid": v(10.55, 1.04) * mm, "end": v(10.56, 1.09) * mm});
            skArc(sketch, "E241", {"start": v(10.56, 1.09) * mm, "mid": v(10.57, 1.13) * mm, "end": v(10.58, 1.17) * mm});
            skArc(sketch, "E242", {"start": v(10.58, 1.17) * mm, "mid": v(10.6, 1.23) * mm, "end": v(10.63, 1.28) * mm});
            skArc(sketch, "E243", {"start": v(10.63, 1.28) * mm, "mid": v(10.69, 1.38) * mm, "end": v(10.76, 1.48) * mm});
            skArc(sketch, "E244", {"start": v(10.76, 1.48) * mm, "mid": v(10.85, 1.57) * mm, "end": v(10.95, 1.65) * mm});
            skArc(sketch, "E245", {"start": v(10.95, 1.65) * mm, "mid": v(11.06, 1.72) * mm, "end": v(11.18, 1.78) * mm});
            skArc(sketch, "E246", {"start": v(11.18, 1.78) * mm, "mid": v(11.3, 1.83) * mm, "end": v(11.43, 1.86) * mm});
            skArc(sketch, "E247", {"start": v(11.43, 1.86) * mm, "mid": v(11.47, 1.87) * mm, "end": v(11.5, 1.87) * mm});
            skArc(sketch, "E248", {"start": v(11.5, 1.87) * mm, "mid": v(11.54, 1.88) * mm, "end": v(11.57, 1.89) * mm});
            skArc(sketch, "E249", {"start": v(11.57, 1.89) * mm, "mid": v(11.6, 1.9) * mm, "end": v(11.63, 1.9) * mm});
            skArc(sketch, "E250", {"start": v(11.63, 1.9) * mm, "mid": v(11.65, 1.9) * mm, "end": v(11.67, 1.9) * mm});
            skArc(sketch, "E251", {"start": v(11.67, 1.9) * mm, "mid": v(11.73, 1.92) * mm, "end": v(11.8, 1.92) * mm});
            skArc(sketch, "E252", {"start": v(11.8, 1.92) * mm, "mid": v(11.92, 1.91) * mm, "end": v(12.05, 1.9) * mm});
            skArc(sketch, "E253", {"start": v(12.05, 1.9) * mm, "mid": v(12.17, 1.9) * mm, "end": v(12.3, 1.88) * mm});
            skArc(sketch, "E254", {"start": v(12.3, 1.88) * mm, "mid": v(12.38, 1.87) * mm, "end": v(12.46, 1.85) * mm});
            skArc(sketch, "E255", {"start": v(-15, 1.62) * mm, "mid": v(-15, 1.15) * mm, "end": v(-14.99, 0.69) * mm});
            skArc(sketch, "E256", {"start": v(-14.99, 0.69) * mm, "mid": v(-14.98, 0.49) * mm, "end": v(-14.97, 0.29) * mm});
            skArc(sketch, "E257", {"start": v(-14.97, 0.29) * mm, "mid": v(-14.95, 0.16) * mm, "end": v(-14.92, 0.03) * mm});
            skArc(sketch, "E258", {"start": v(-14.92, 0.03) * mm, "mid": v(-14.87, -0.1) * mm, "end": v(-14.81, -0.2) * mm});
            skArc(sketch, "E259", {"start": v(-14.81, -0.2) * mm, "mid": v(-14.75, -0.3) * mm, "end": v(-14.68, -0.4) * mm});
            skArc(sketch, "E260", {"start": v(-14.68, -0.4) * mm, "mid": v(-14.58, -0.5) * mm, "end": v(-14.47, -0.6) * mm});
            skArc(sketch, "E261", {"start": v(-14.47, -0.6) * mm, "mid": v(-14.35, -0.7) * mm, "end": v(-14.23, -0.8) * mm});
            skArc(sketch, "E262", {"start": v(-14.23, -0.8) * mm, "mid": v(-14.1, -0.87) * mm, "end": v(-13.98, -0.94) * mm});
            skArc(sketch, "E263", {"start": v(-13.98, -0.94) * mm, "mid": v(-13.79, -1.02) * mm, "end": v(-13.59, -1.1) * mm});
            skArc(sketch, "E264", {"start": v(-13.59, -1.1) * mm, "mid": v(-13.37, -1.16) * mm, "end": v(-13.16, -1.2) * mm});
            skArc(sketch, "E265", {"start": v(-13.16, -1.2) * mm, "mid": v(-12.92, -1.25) * mm, "end": v(-12.67, -1.27) * mm});
            skArc(sketch, "E266", {"start": v(-12.67, -1.27) * mm, "mid": v(-12.4, -1.29) * mm, "end": v(-12.12, -1.3) * mm});
            skArc(sketch, "E267", {"start": v(-12.12, -1.3) * mm, "mid": v(-11.62, -1.27) * mm, "end": v(-11.11, -1.2) * mm});
            skArc(sketch, "E268", {"start": v(-11.11, -1.2) * mm, "mid": v(-10.7, -1.1) * mm, "end": v(-10.3, -0.93) * mm});
            skArc(sketch, "E269", {"start": v(-10.3, -0.93) * mm, "mid": v(-9.98, -0.74) * mm, "end": v(-9.7, -0.5) * mm});
            skArc(sketch, "E270", {"start": v(-9.7, -0.5) * mm, "mid": v(-9.5, -0.23) * mm, "end": v(-9.36, 0.08) * mm});
            skArc(sketch, "E271", {"start": v(-9.36, 0.08) * mm, "mid": v(-9.33, 0.16) * mm, "end": v(-9.32, 0.24) * mm});
            skArc(sketch, "E272", {"start": v(-9.32, 0.24) * mm, "mid": v(-9.3, 0.35) * mm, "end": v(-9.3, 0.45) * mm});
            skArc(sketch, "E273", {"start": v(-9.3, 0.45) * mm, "mid": v(-9.3, 0.62) * mm, "end": v(-9.29, 0.79) * mm});
            skArc(sketch, "E274", {"start": v(-9.29, 0.79) * mm, "mid": v(-9.28, 1.2) * mm, "end": v(-9.28, 1.6) * mm});
            skLineSegment(sketch, "E275", {"start": v(-9.28, 1.6) * mm, "end": v(-9.26, 2.93) * mm});
            skLineSegment(sketch, "E276", {"start": v(-9.26, 2.93) * mm, "end": v(-10.1, 2.93) * mm});
            skLineSegment(sketch, "E277", {"start": v(-10.1, 2.93) * mm, "end": v(-10.93, 2.93) * mm});
            skLineSegment(sketch, "E278", {"start": v(-10.93, 2.93) * mm, "end": v(-10.93, 1.87) * mm});
            skArc(sketch, "E279", {"start": v(-10.93, 1.87) * mm, "mid": v(-10.93, 1.43) * mm, "end": v(-10.94, 1) * mm});
            skArc(sketch, "E280", {"start": v(-10.94, 1) * mm, "mid": v(-10.95, 0.78) * mm, "end": v(-10.98, 0.57) * mm});
            skArc(sketch, "E281", {"start": v(-10.98, 0.57) * mm, "mid": v(-11.02, 0.43) * mm, "end": v(-11.07, 0.3) * mm});
            skArc(sketch, "E282", {"start": v(-11.07, 0.3) * mm, "mid": v(-11.16, 0.18) * mm, "end": v(-11.25, 0.07) * mm});
            skArc(sketch, "E283", {"start": v(-11.25, 0.07) * mm, "mid": v(-11.33, 0) * mm, "end": v(-11.4, -0.06) * mm});
            skArc(sketch, "E284", {"start": v(-11.4, -0.06) * mm, "mid": v(-11.5, -0.1) * mm, "end": v(-11.59, -0.14) * mm});
            skArc(sketch, "E285", {"start": v(-11.59, -0.14) * mm, "mid": v(-11.7, -0.18) * mm, "end": v(-11.8, -0.2) * mm});
            skArc(sketch, "E286", {"start": v(-11.8, -0.2) * mm, "mid": v(-11.94, -0.22) * mm, "end": v(-12.08, -0.22) * mm});
            skArc(sketch, "E287", {"start": v(-12.08, -0.22) * mm, "mid": v(-12.27, -0.22) * mm, "end": v(-12.46, -0.2) * mm});
            skArc(sketch, "E288", {"start": v(-12.46, -0.2) * mm, "mid": v(-12.62, -0.17) * mm, "end": v(-12.78, -0.12) * mm});
            skArc(sketch, "E289", {"start": v(-12.78, -0.12) * mm, "mid": v(-12.9, -0.04) * mm, "end": v(-13.02, 0.05) * mm});
            skArc(sketch, "E290", {"start": v(-13.02, 0.05) * mm, "mid": v(-13.12, 0.16) * mm, "end": v(-13.2, 0.3) * mm});
            skArc(sketch, "E291", {"start": v(-13.2, 0.3) * mm, "mid": v(-13.25, 0.4) * mm, "end": v(-13.29, 0.51) * mm});
            skArc(sketch, "E292", {"start": v(-13.29, 0.51) * mm, "mid": v(-13.32, 0.64) * mm, "end": v(-13.34, 0.77) * mm});
            skArc(sketch, "E293", {"start": v(-13.34, 0.77) * mm, "mid": v(-13.35, 0.97) * mm, "end": v(-13.36, 1.17) * mm});
            skArc(sketch, "E294", {"start": v(-13.36, 1.17) * mm, "mid": v(-13.36, 1.54) * mm, "end": v(-13.37, 1.92) * mm});
            skLineSegment(sketch, "E295", {"start": v(-13.37, 1.92) * mm, "end": v(-13.37, 2.93) * mm});
            skLineSegment(sketch, "E296", {"start": v(-13.37, 2.93) * mm, "end": v(-14.18, 2.93) * mm});
            skLineSegment(sketch, "E297", {"start": v(-14.18, 2.93) * mm, "end": v(-15, 2.93) * mm});
            skLineSegment(sketch, "E298", {"start": v(-15, 2.93) * mm, "end": v(-15, 1.62) * mm});
            skArc(sketch, "E299", {"start": v(-8.83, 2.9) * mm, "mid": v(-8.82, 2.88) * mm, "end": v(-8.82, 2.87) * mm});
            skArc(sketch, "E300", {"start": v(-8.82, 2.87) * mm, "mid": v(-8.64, 2.58) * mm, "end": v(-8.47, 2.28) * mm});
            skArc(sketch, "E301", {"start": v(-8.47, 2.28) * mm, "mid": v(-8.28, 1.95) * mm, "end": v(-8.08, 1.62) * mm});
            skArc(sketch, "E302", {"start": v(-8.08, 1.62) * mm, "mid": v(-7.86, 1.24) * mm, "end": v(-7.63, 0.85) * mm});
            skLineSegment(sketch, "E303", {"start": v(-7.63, 0.85) * mm, "end": v(-6.44, -1.17) * mm});
            skLineSegment(sketch, "E304", {"start": v(-6.44, -1.17) * mm, "end": v(-5.9, -1.17) * mm});
            skLineSegment(sketch, "E305", {"start": v(-5.9, -1.17) * mm, "end": v(-5.35, -1.17) * mm});
            skLineSegment(sketch, "E306", {"start": v(-5.35, -1.17) * mm, "end": v(-4.15, 0.86) * mm});
            skArc(sketch, "E307", {"start": v(-4.15, 0.86) * mm, "mid": v(-3.92, 1.25) * mm, "end": v(-3.7, 1.64) * mm});
            skArc(sketch, "E308", {"start": v(-3.7, 1.64) * mm, "mid": v(-3.5, 1.97) * mm, "end": v(-3.3, 2.3) * mm});
            skArc(sketch, "E309", {"start": v(-3.3, 2.3) * mm, "mid": v(-3.13, 2.6) * mm, "end": v(-2.96, 2.9) * mm});
            skArc(sketch, "E310", {"start": v(-2.96, 2.9) * mm, "mid": v(-2.95, 2.9) * mm, "end": v(-2.95, 2.9) * mm});
            skArc(sketch, "E311", {"start": v(-2.95, 2.9) * mm, "mid": v(-2.96, 2.91) * mm, "end": v(-2.96, 2.91) * mm});
            skArc(sketch, "E312", {"start": v(-2.96, 2.91) * mm, "mid": v(-3.07, 2.92) * mm, "end": v(-3.18, 2.92) * mm});
            skArc(sketch, "E313", {"start": v(-3.18, 2.92) * mm, "mid": v(-3.3, 2.92) * mm, "end": v(-3.42, 2.93) * mm});
            skArc(sketch, "E314", {"start": v(-3.42, 2.93) * mm, "mid": v(-3.57, 2.93) * mm, "end": v(-3.71, 2.93) * mm});
            skLineSegment(sketch, "E315", {"start": v(-3.71, 2.93) * mm, "end": v(-4.48, 2.93) * mm});
            skLineSegment(sketch, "E316", {"start": v(-4.48, 2.93) * mm, "end": v(-5.17, 1.74) * mm});
            skArc(sketch, "E317", {"start": v(-5.17, 1.74) * mm, "mid": v(-5.3, 1.51) * mm, "end": v(-5.44, 1.28) * mm});
            skArc(sketch, "E318", {"start": v(-5.44, 1.28) * mm, "mid": v(-5.56, 1.1) * mm, "end": v(-5.67, 0.9) * mm});
            skArc(sketch, "E319", {"start": v(-5.67, 0.9) * mm, "mid": v(-5.77, 0.73) * mm, "end": v(-5.88, 0.56) * mm});
            skArc(sketch, "E320", {"start": v(-5.88, 0.56) * mm, "mid": v(-5.88, 0.55) * mm, "end": v(-5.9, 0.55) * mm});
            skArc(sketch, "E321", {"start": v(-5.9, 0.55) * mm, "mid": v(-5.9, 0.55) * mm, "end": v(-5.9, 0.56) * mm});
            skArc(sketch, "E322", {"start": v(-5.9, 0.56) * mm, "mid": v(-6, 0.73) * mm, "end": v(-6.11, 0.9) * mm});
            skArc(sketch, "E323", {"start": v(-6.11, 0.9) * mm, "mid": v(-6.23, 1.1) * mm, "end": v(-6.34, 1.28) * mm});
            skArc(sketch, "E324", {"start": v(-6.34, 1.28) * mm, "mid": v(-6.48, 1.51) * mm, "end": v(-6.61, 1.74) * mm});
            skLineSegment(sketch, "E325", {"start": v(-6.61, 1.74) * mm, "end": v(-7.3, 2.93) * mm});
            skLineSegment(sketch, "E326", {"start": v(-7.3, 2.93) * mm, "end": v(-8.07, 2.93) * mm});
            skArc(sketch, "E327", {"start": v(-8.07, 2.93) * mm, "mid": v(-8.23, 2.93) * mm, "end": v(-8.4, 2.92) * mm});
            skArc(sketch, "E328", {"start": v(-8.4, 2.92) * mm, "mid": v(-8.51, 2.92) * mm, "end": v(-8.63, 2.92) * mm});
            skArc(sketch, "E329", {"start": v(-8.63, 2.92) * mm, "mid": v(-8.73, 2.91) * mm, "end": v(-8.82, 2.9) * mm});
            skArc(sketch, "E330", {"start": v(-8.82, 2.9) * mm, "mid": v(-8.83, 2.9) * mm, "end": v(-8.83, 2.9) * mm});
            skSolve(sketch);
        }
        {
            var Q0;
            Q0 = qSketchRegion(id + "F3", true);
            extrude(context, id + "F4", {"entities" : qUnion([Q0]), "operationType" : NewBodyOperationType.REMOVE, "oppositeDirection" : true, "depth" : 1 * mm, "offsetDistance" : 25 * mm});
        }
    });
